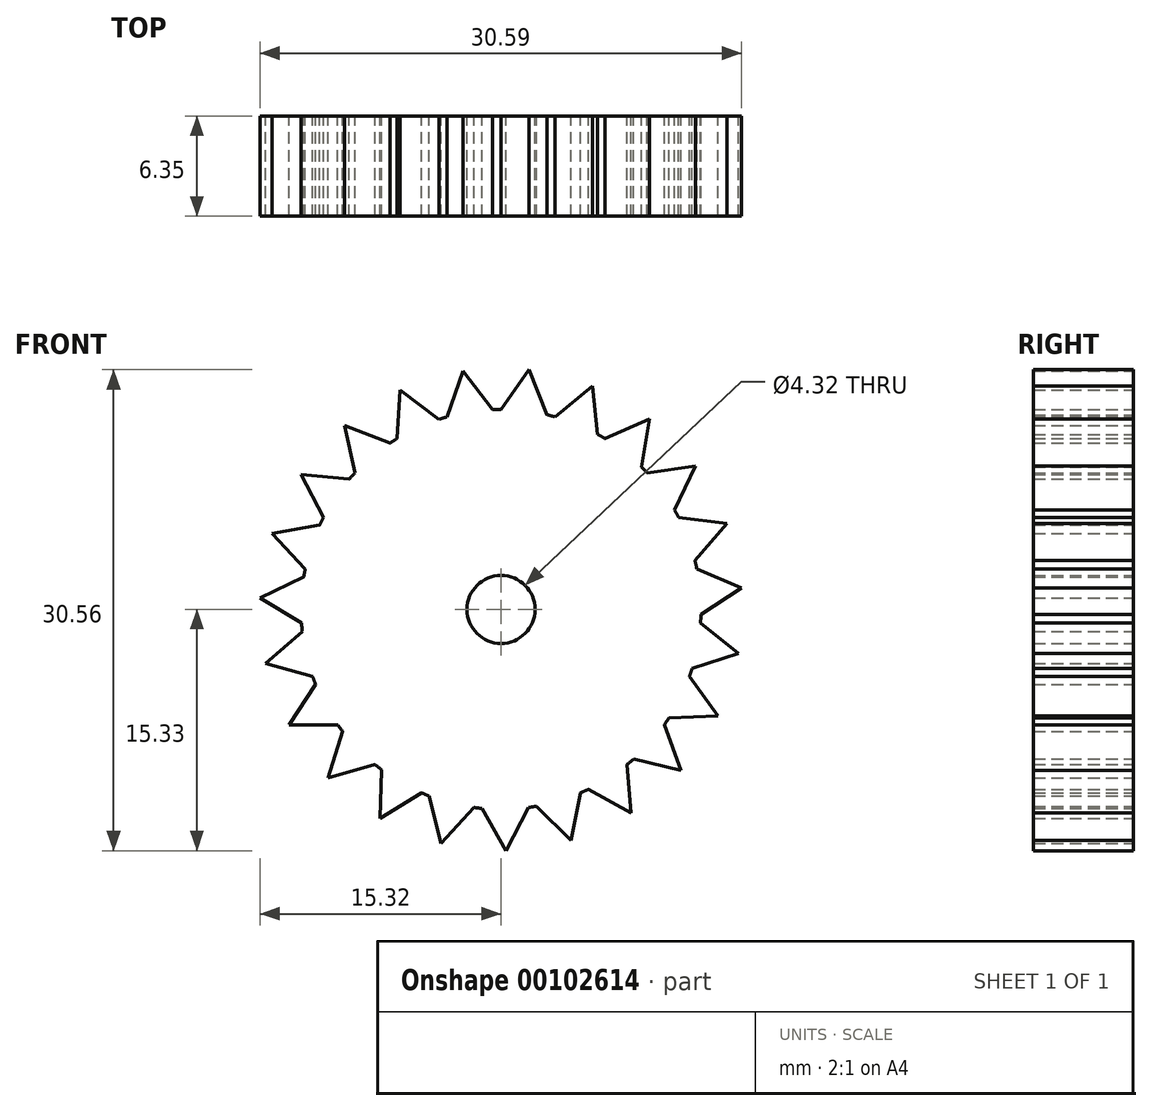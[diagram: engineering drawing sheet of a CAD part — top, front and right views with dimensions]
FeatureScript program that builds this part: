
annotation { "Feature Type Name" : "Feature", "Feature Type Description" : "" }
export const myFeature = defineFeature(function(context is Context, id is Id, definition is map)
    precondition{}
    {
        {
            var Q0;
            Q0=qCreatedBy(makeId("Front.planeOp"),FACE);
            var sketch = newSketch(context, id + "F0", { "sketchPlane" : qUnion([Q0])});
            skCircle(sketch, "E0", {"center": v(0, 0) * mm, "radius": 2.16 * mm});
            skCircle(sketch, "E1", {"center": v(0, 0) * mm, "radius": 12.7 * mm});
            skLineSegment(sketch, "E2", {"start": v(0, 12.7) * mm, "end": v(1.76, 15.23) * mm});
            skLineSegment(sketch, "E3", {"start": v(1.76, 15.23) * mm, "end": v(2.9, 12.36) * mm});
            skLineSegment(sketch, "E4.1.0", {"start": v(-3.43, 12.23) * mm, "end": v(-2.41, 15.14) * mm});
            skLineSegment(sketch, "E4.1.1", {"start": v(-2.41, 15.14) * mm, "end": v(-0.54, 12.69) * mm});
            skLineSegment(sketch, "E4.2.0", {"start": v(-6.6, 10.85) * mm, "end": v(-6.4, 13.93) * mm});
            skLineSegment(sketch, "E4.2.1", {"start": v(-6.4, 13.93) * mm, "end": v(-3.94, 12.07) * mm});
            skLineSegment(sketch, "E4.3.0", {"start": v(-9.28, 8.67) * mm, "end": v(-9.93, 11.68) * mm});
            skLineSegment(sketch, "E4.3.1", {"start": v(-9.93, 11.68) * mm, "end": v(-7.05, 10.56) * mm});
            skLineSegment(sketch, "E4.4.0", {"start": v(-11.28, 5.84) * mm, "end": v(-12.71, 8.57) * mm});
            skLineSegment(sketch, "E4.4.1", {"start": v(-12.71, 8.57) * mm, "end": v(-9.64, 8.27) * mm});
            skLineSegment(sketch, "E4.5.0", {"start": v(-12.43, 2.58) * mm, "end": v(-14.56, 4.82) * mm});
            skLineSegment(sketch, "E4.5.1", {"start": v(-14.56, 4.82) * mm, "end": v(-11.51, 5.36) * mm});
            skLineSegment(sketch, "E4.6.0", {"start": v(-12.67, -0.87) * mm, "end": v(-15.32, 0.72) * mm});
            skLineSegment(sketch, "E4.6.1", {"start": v(-15.32, 0.72) * mm, "end": v(-12.53, 2.06) * mm});
            skLineSegment(sketch, "E4.7.0", {"start": v(-11.97, -4.25) * mm, "end": v(-14.94, -3.44) * mm});
            skLineSegment(sketch, "E4.7.1", {"start": v(-14.94, -3.44) * mm, "end": v(-12.62, -1.4) * mm});
            skLineSegment(sketch, "E4.8.0", {"start": v(-10.38, -7.32) * mm, "end": v(-13.46, -7.35) * mm});
            skLineSegment(sketch, "E4.8.1", {"start": v(-13.46, -7.35) * mm, "end": v(-11.78, -4.76) * mm});
            skLineSegment(sketch, "E4.9.0", {"start": v(-8.01, -9.85) * mm, "end": v(-10.98, -10.7) * mm});
            skLineSegment(sketch, "E4.9.1", {"start": v(-10.98, -10.7) * mm, "end": v(-10.06, -7.76) * mm});
            skLineSegment(sketch, "E5.1.10.0", {"start": v(-5.06, -11.65) * mm, "end": v(-7.68, -13.27) * mm});
            skLineSegment(sketch, "E5.3.10.0", {"start": v(-7.68, -13.27) * mm, "end": v(-7.6, -10.18) * mm});
            skLineSegment(sketch, "E5.1.11.0", {"start": v(-1.73, -12.58) * mm, "end": v(-3.82, -14.85) * mm});
            skLineSegment(sketch, "E5.3.11.0", {"start": v(-3.82, -14.85) * mm, "end": v(-4.56, -11.85) * mm});
            skLineSegment(sketch, "E5.1.12.0", {"start": v(1.73, -12.58) * mm, "end": v(0.33, -15.33) * mm});
            skLineSegment(sketch, "E5.3.12.0", {"start": v(0.33, -15.33) * mm, "end": v(-1.2, -12.64) * mm});
            skLineSegment(sketch, "E5.1.13.0", {"start": v(5.06, -11.65) * mm, "end": v(4.45, -14.67) * mm});
            skLineSegment(sketch, "E5.3.13.0", {"start": v(4.45, -14.67) * mm, "end": v(2.26, -12.5) * mm});
            skLineSegment(sketch, "E5.1.14.0", {"start": v(8.01, -9.85) * mm, "end": v(8.25, -12.93) * mm});
            skLineSegment(sketch, "E5.3.14.0", {"start": v(8.25, -12.93) * mm, "end": v(5.55, -11.42) * mm});
            skLineSegment(sketch, "E6.1.15.0", {"start": v(10.38, -7.32) * mm, "end": v(11.43, -10.22) * mm});
            skLineSegment(sketch, "E6.3.15.0", {"start": v(11.43, -10.22) * mm, "end": v(8.42, -9.5) * mm});
            skLineSegment(sketch, "E7.1.16.0", {"start": v(11.97, -4.25) * mm, "end": v(13.76, -6.76) * mm});
            skLineSegment(sketch, "E7.3.16.0", {"start": v(13.76, -6.76) * mm, "end": v(10.68, -6.88) * mm});
            skLineSegment(sketch, "E7.1.17.0", {"start": v(12.67, -0.87) * mm, "end": v(15.08, -2.8) * mm});
            skLineSegment(sketch, "E7.3.17.0", {"start": v(15.08, -2.8) * mm, "end": v(12.14, -3.74) * mm});
            skLineSegment(sketch, "E8.1.18.0", {"start": v(12.43, 2.58) * mm, "end": v(15.27, 1.38) * mm});
            skLineSegment(sketch, "E8.3.18.0", {"start": v(15.27, 1.38) * mm, "end": v(12.7, -0.33) * mm});
            skLineSegment(sketch, "E8.1.19.0", {"start": v(11.28, 5.84) * mm, "end": v(14.33, 5.44) * mm});
            skLineSegment(sketch, "E8.3.19.0", {"start": v(14.33, 5.44) * mm, "end": v(12.31, 3.1) * mm});
            skLineSegment(sketch, "E9.1.20.0", {"start": v(9.28, 8.67) * mm, "end": v(12.33, 9.1) * mm});
            skLineSegment(sketch, "E9.3.20.0", {"start": v(12.33, 9.1) * mm, "end": v(11.02, 6.31) * mm});
            skLineSegment(sketch, "E9.1.21.0", {"start": v(6.6, 10.85) * mm, "end": v(9.42, 12.1) * mm});
            skLineSegment(sketch, "E9.3.21.0", {"start": v(9.42, 12.1) * mm, "end": v(8.9, 9.05) * mm});
            skLineSegment(sketch, "E10.1.22.0", {"start": v(3.43, 12.23) * mm, "end": v(5.8, 14.2) * mm});
            skLineSegment(sketch, "E10.3.22.0", {"start": v(5.8, 14.2) * mm, "end": v(6.13, 11.12) * mm});
            skSolve(sketch);
        }
        {
            var Q0;
            Q0=makeQuery(id+"F0.imprint","IMPRINT",FACE,{"disambiguationData":[TD([[makeQuery(id+"F0.imprint","IMPRINT",EDGE,{"derivedFrom":sQuery(id+"F0.wireOp",EDGE,"E0")}),-1.0]])]});
            var Q1;
            {var subQ0=sQuery(id+"F0.wireOp",EDGE,"E4.6.0");Q1=makeQuery(id+"F0.imprint","IMPRINT",FACE,{"disambiguationData":[TD([[makeQuery(id+"F0.imprint","IMPRINT",EDGE,{"derivedFrom":subQ0}),-1.0]])]});}
            var Q2;
            {var subQ0=sQuery(id+"F0.wireOp",EDGE,"E4.5.0");Q2=makeQuery(id+"F0.imprint","IMPRINT",FACE,{"disambiguationData":[TD([[makeQuery(id+"F0.imprint","IMPRINT",EDGE,{"derivedFrom":subQ0}),-1.0]])]});}
            var Q3;
            {var subQ0=sQuery(id+"F0.wireOp",EDGE,"E4.4.0");Q3=makeQuery(id+"F0.imprint","IMPRINT",FACE,{"disambiguationData":[TD([[makeQuery(id+"F0.imprint","IMPRINT",EDGE,{"derivedFrom":subQ0}),-1.0]])]});}
            var Q4;
            {var subQ0=sQuery(id+"F0.wireOp",EDGE,"E4.3.0");Q4=makeQuery(id+"F0.imprint","IMPRINT",FACE,{"disambiguationData":[TD([[makeQuery(id+"F0.imprint","IMPRINT",EDGE,{"derivedFrom":subQ0}),-1.0]])]});}
            var Q5;
            {var subQ0=sQuery(id+"F0.wireOp",EDGE,"E4.2.0");Q5=makeQuery(id+"F0.imprint","IMPRINT",FACE,{"disambiguationData":[TD([[makeQuery(id+"F0.imprint","IMPRINT",EDGE,{"derivedFrom":subQ0}),-1.0]])]});}
            var Q6;
            {var subQ0=sQuery(id+"F0.wireOp",EDGE,"E4.1.0");Q6=makeQuery(id+"F0.imprint","IMPRINT",FACE,{"disambiguationData":[TD([[makeQuery(id+"F0.imprint","IMPRINT",EDGE,{"derivedFrom":subQ0}),-1.0]])]});}
            var Q7;
            {var subQ0=sQuery(id+"F0.wireOp",EDGE,"E2");Q7=makeQuery(id+"F0.imprint","IMPRINT",FACE,{"disambiguationData":[TD([[makeQuery(id+"F0.imprint","IMPRINT",EDGE,{"derivedFrom":subQ0}),-1.0]])]});}
            var Q8;
            {var subQ0=sQuery(id+"F0.wireOp",EDGE,"E10.1.22.0");Q8=makeQuery(id+"F0.imprint","IMPRINT",FACE,{"disambiguationData":[TD([[makeQuery(id+"F0.imprint","IMPRINT",EDGE,{"derivedFrom":subQ0}),-1.0]])]});}
            var Q9;
            {var subQ0=sQuery(id+"F0.wireOp",EDGE,"E9.1.21.0");Q9=makeQuery(id+"F0.imprint","IMPRINT",FACE,{"disambiguationData":[TD([[makeQuery(id+"F0.imprint","IMPRINT",EDGE,{"derivedFrom":subQ0}),-1.0]])]});}
            var Q10;
            {var subQ0=sQuery(id+"F0.wireOp",EDGE,"E9.1.20.0");Q10=makeQuery(id+"F0.imprint","IMPRINT",FACE,{"disambiguationData":[TD([[makeQuery(id+"F0.imprint","IMPRINT",EDGE,{"derivedFrom":subQ0}),-1.0]])]});}
            var Q11;
            {var subQ0=sQuery(id+"F0.wireOp",EDGE,"E8.1.19.0");Q11=makeQuery(id+"F0.imprint","IMPRINT",FACE,{"disambiguationData":[TD([[makeQuery(id+"F0.imprint","IMPRINT",EDGE,{"derivedFrom":subQ0}),-1.0]])]});}
            var Q12;
            {var subQ0=sQuery(id+"F0.wireOp",EDGE,"E8.1.18.0");Q12=makeQuery(id+"F0.imprint","IMPRINT",FACE,{"disambiguationData":[TD([[makeQuery(id+"F0.imprint","IMPRINT",EDGE,{"derivedFrom":subQ0}),-1.0]])]});}
            var Q13;
            {var subQ0=sQuery(id+"F0.wireOp",EDGE,"E7.1.17.0");Q13=makeQuery(id+"F0.imprint","IMPRINT",FACE,{"disambiguationData":[TD([[makeQuery(id+"F0.imprint","IMPRINT",EDGE,{"derivedFrom":subQ0}),-1.0]])]});}
            var Q14;
            {var subQ0=sQuery(id+"F0.wireOp",EDGE,"E7.1.16.0");Q14=makeQuery(id+"F0.imprint","IMPRINT",FACE,{"disambiguationData":[TD([[makeQuery(id+"F0.imprint","IMPRINT",EDGE,{"derivedFrom":subQ0}),-1.0]])]});}
            var Q15;
            {var subQ0=sQuery(id+"F0.wireOp",EDGE,"E6.1.15.0");Q15=makeQuery(id+"F0.imprint","IMPRINT",FACE,{"disambiguationData":[TD([[makeQuery(id+"F0.imprint","IMPRINT",EDGE,{"derivedFrom":subQ0}),-1.0]])]});}
            var Q16;
            {var subQ0=sQuery(id+"F0.wireOp",EDGE,"E5.1.14.0");Q16=makeQuery(id+"F0.imprint","IMPRINT",FACE,{"disambiguationData":[TD([[makeQuery(id+"F0.imprint","IMPRINT",EDGE,{"derivedFrom":subQ0}),-1.0]])]});}
            var Q17;
            {var subQ0=sQuery(id+"F0.wireOp",EDGE,"E5.1.13.0");Q17=makeQuery(id+"F0.imprint","IMPRINT",FACE,{"disambiguationData":[TD([[makeQuery(id+"F0.imprint","IMPRINT",EDGE,{"derivedFrom":subQ0}),-1.0]])]});}
            var Q18;
            {var subQ0=sQuery(id+"F0.wireOp",EDGE,"E5.1.12.0");Q18=makeQuery(id+"F0.imprint","IMPRINT",FACE,{"disambiguationData":[TD([[makeQuery(id+"F0.imprint","IMPRINT",EDGE,{"derivedFrom":subQ0}),-1.0]])]});}
            var Q19;
            {var subQ0=sQuery(id+"F0.wireOp",EDGE,"E5.1.11.0");Q19=makeQuery(id+"F0.imprint","IMPRINT",FACE,{"disambiguationData":[TD([[makeQuery(id+"F0.imprint","IMPRINT",EDGE,{"derivedFrom":subQ0}),-1.0]])]});}
            var Q20;
            {var subQ0=sQuery(id+"F0.wireOp",EDGE,"E5.1.10.0");Q20=makeQuery(id+"F0.imprint","IMPRINT",FACE,{"disambiguationData":[TD([[makeQuery(id+"F0.imprint","IMPRINT",EDGE,{"derivedFrom":subQ0}),-1.0]])]});}
            var Q21;
            {var subQ0=sQuery(id+"F0.wireOp",EDGE,"E4.9.0");Q21=makeQuery(id+"F0.imprint","IMPRINT",FACE,{"disambiguationData":[TD([[makeQuery(id+"F0.imprint","IMPRINT",EDGE,{"derivedFrom":subQ0}),-1.0]])]});}
            var Q22;
            {var subQ0=sQuery(id+"F0.wireOp",EDGE,"E4.8.0");Q22=makeQuery(id+"F0.imprint","IMPRINT",FACE,{"disambiguationData":[TD([[makeQuery(id+"F0.imprint","IMPRINT",EDGE,{"derivedFrom":subQ0}),-1.0]])]});}
            var Q23;
            {var subQ0=sQuery(id+"F0.wireOp",EDGE,"E4.7.0");Q23=makeQuery(id+"F0.imprint","IMPRINT",FACE,{"disambiguationData":[TD([[makeQuery(id+"F0.imprint","IMPRINT",EDGE,{"derivedFrom":subQ0}),-1.0]])]});}
            extrude(context, id + "F1", {"entities" : qUnion([Q0, Q1, Q2, Q3, Q4, Q5, Q6, Q7, Q8, Q9, Q10, Q11, Q12, Q13, Q14, Q15, Q16, Q17, Q18, Q19, Q20, Q21, Q22, Q23]), "depth" : 6.35 * mm});
        }
    });
